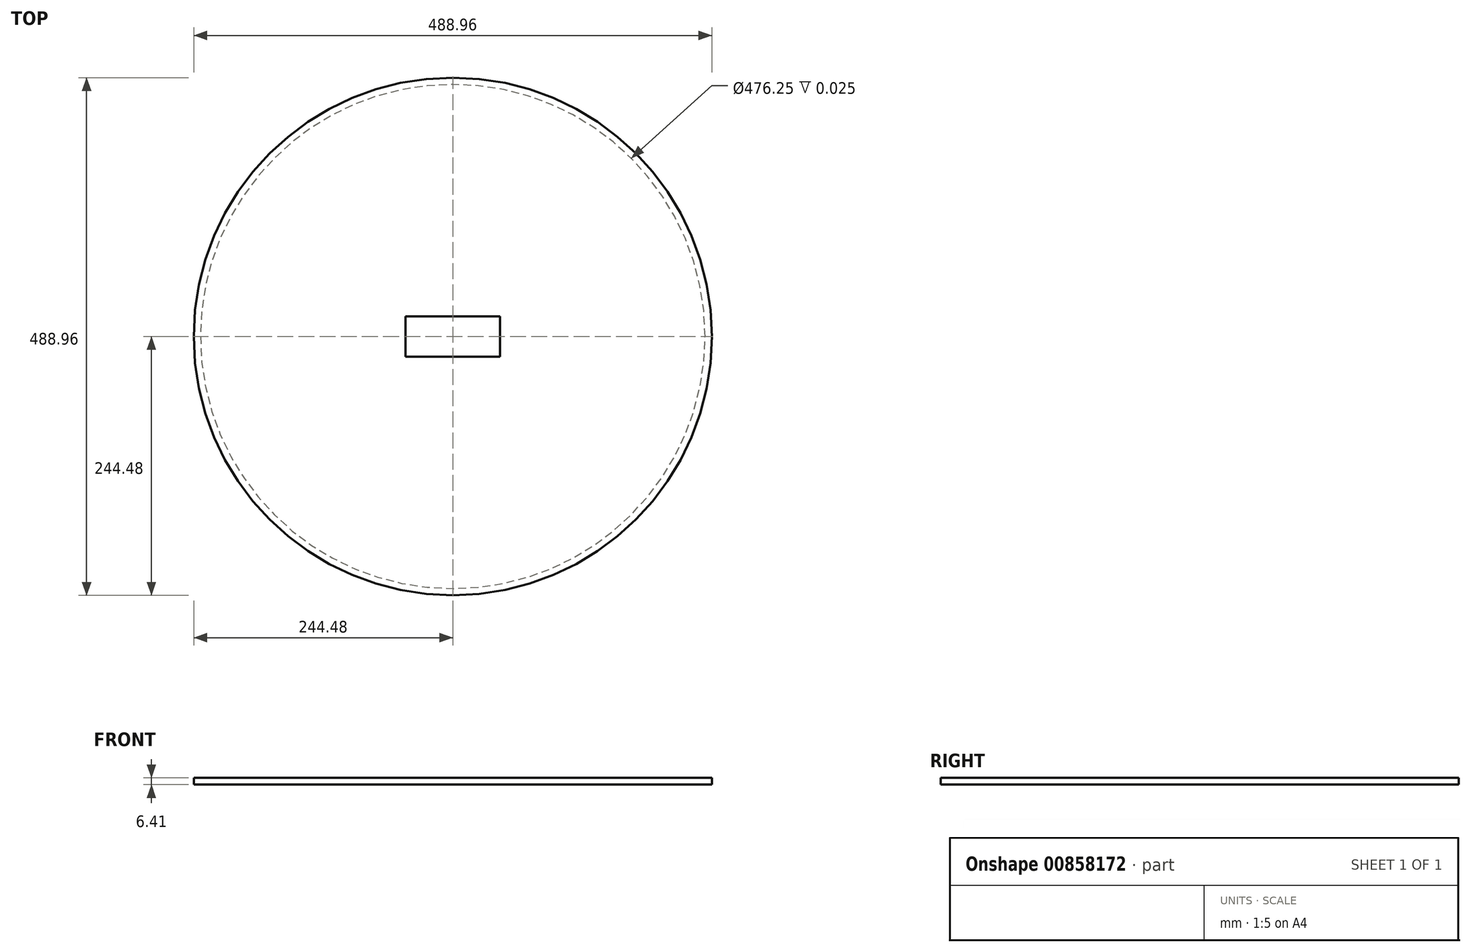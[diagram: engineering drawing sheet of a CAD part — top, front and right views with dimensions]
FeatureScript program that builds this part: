
annotation { "Feature Type Name" : "Feature", "Feature Type Description" : "" }
export const myFeature = defineFeature(function(context is Context, id is Id, definition is map)
    precondition{}
    {
        {
            var Q0;
            Q0=qCreatedBy(makeId("Front.planeOp"),FACE);
            var sketch = newSketch(context, id + "F0", { "sketchPlane" : qUnion([Q0])});
            skLineSegment(sketch, "E0.bottom", {"start": v(0, 0) * mm, "end": v(244.48, 0) * mm});
            skLineSegment(sketch, "E0.top", {"start": v(0, -6.35) * mm, "end": v(238.13, -6.35) * mm});
            skLineSegment(sketch, "E0.left", {"start": v(0, 0) * mm, "end": v(0, -6.35) * mm});
            skLineSegment(sketch, "E1.top", {"start": v(244.48, -6.38) * mm, "end": v(238.13, -6.38) * mm});
            skLineSegment(sketch, "E1.right", {"start": v(238.13, -6.35) * mm, "end": v(238.13, -6.38) * mm});
            skLineSegment(sketch, "E2", {"start": v(244.48, 0) * mm, "end": v(244.48, -6.38) * mm});
            skLineSegment(sketch, "E3", {"start": v(0, 0) * mm, "end": v(0, -85.66) * mm, "construction": true});
            skSolve(sketch);
        }
        {
            var Q0;
            Q0 = qSketchRegion(id + "F0", true);
            var Q1;
            Q1=sQuery(id+"F0.wireOp",EDGE,"E3");
            revolve(context, id + "F1", {"surfaceOperationType" : NewSurfaceOperationType.NEW, "entities" : qUnion([Q0]), "axis" : qUnion([Q1]), "revolveType" : RevolveType.FULL});
        }
        {
            var Q0;
            Q0=makeQuery(id+"F1.opRevolve","SWEPT_FACE",FACE,{"disambiguationData":[OSD([sQuery(id+"F0.wireOp",EDGE,"E0.bottom")])]});
            var sketch = newSketch(context, id + "F2", { "sketchPlane" : qUnion([Q0])});
            skLineSegment(sketch, "E4.bottom", {"start": v(44.45, 19.05) * mm, "end": v(-44.45, 19.05) * mm});
            skLineSegment(sketch, "E4.top", {"start": v(44.45, -19.05) * mm, "end": v(-44.45, -19.05) * mm});
            skLineSegment(sketch, "E4.left", {"start": v(44.45, 19.05) * mm, "end": v(44.45, -19.05) * mm});
            skLineSegment(sketch, "E4.right", {"start": v(-44.45, 19.05) * mm, "end": v(-44.45, -19.05) * mm});
            skPoint(sketch, "E4.middle", {"position": v(0, 0) * mm});
            skSolve(sketch);
        }
        {
            var Q0;
            Q0 = qSketchRegion(id + "F2", true);
            extrude(context, id + "F3", {"entities" : qUnion([Q0]), "operationType" : NewBodyOperationType.ADD, "depth" : 0.03 * mm, "offsetDistance" : 25.4 * mm});
        }
    });
